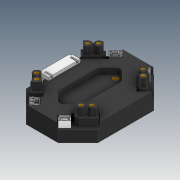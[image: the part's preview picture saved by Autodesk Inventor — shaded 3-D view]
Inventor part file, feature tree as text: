
AUTODESK INVENTOR PART (.ipt)
format: ipt  version: 2020 (Build 240168000, 168)  size: 708,608 bytes
history: native  units: mm
features: sketch x16, extrude x15, pattern_circular x4, projected_geometry x4, fillet x3, other x2, plane x1, mirror x1
ambient origin geometry x8: Origin, YZ Plane, XZ Plane, XY Plane, X Axis, Y Axis, Z Axis, Center Point
bodies: Solid1 (feature_tree)
feature tree (46):
  extrude  "Extrusion1"  Depth=60.0mm
  extrude  "Extrusion2"  Depth=20.0mm
  extrude  "Extrusion3"  Depth=5.3mm
  sketch  "Sketch4"  dims[d9=2.5mm]
  other  "Work Axis1"
  fillet  "Fillet1"  Radius=11.0mm
  fillet  "Fillet2"  Radius=8.5mm
  pattern_circular  "Circular Pattern1"  Count=2 Angle=270.0deg
  pattern_circular  "Circular Pattern2"  Count=2 Angle=360.0deg
  extrude  "Extrusion4"  Depth=5.8mm
  sketch  "Sketch6"  dims[d11=0.5mm]
  extrude  "Extrusion5"  Depth=4.15mm TaperAngle=0.0deg
  extrude  "Extrusion6"  Depth=0.3mm
  extrude  "Extrusion7"  Depth=1.0mm
  plane  "Work Plane1"
  mirror  "Mirror1"
  sketch  "Sketch8"  dims[d15=4.8mm]
  other  "Work Axis2"
  pattern_circular  "Circular Pattern3"  [2 undecoded]
  pattern_circular  "Circular Pattern4"  [2 undecoded]
  extrude  "Extrusion8"  Depth=1.6mm
  extrude  "Extrusion9"  Depth=0.3mm
  extrude  "Extrusion10"  Depth=0.3mm
  extrude  "Extrusion11"  Depth=0.3mm
  extrude  "Extrusion12"  Depth=0.3mm
  extrude  "Extrusion13"  Depth=0.3mm
  extrude  "Extrusion14"  Depth=0.6mm
  fillet  "Fillet3"  Radius=0.6mm
  extrude  "Extrusion15"  Depth=0.3mm
  sketch  "Sketch1"  dims[d0=45.0mm d1=60.0mm]
  sketch  "Sketch2"  dims[d2=20.0mm d3=35.0mm]
  sketch  "Sketch3"  dims[d4=6.8mm d5=0.0mm d6=5.3mm d7=11.0mm d8=8.5mm]
  projected_geometry  "Projected Loop1"
  sketch  "Sketch5"  dims[d10=2.0mm]
  projected_geometry  "Projected Loop2"
  sketch  "Sketch7"  dims[d12=5.2mm d13=0.0mm]
  sketch  "Sketch9"  dims[d16=2.5mm]
  sketch  "Sketch10"  dims[d17=0.5mm]
  projected_geometry  "Projected Loop3"
  sketch  "Sketch11"  dims[d18=5.2mm d19=0.0mm]
  sketch  "Sketch12"  dims[d20=0.2mm]
  sketch  "Sketch13"  dims[d21=0.2mm d22=20.0mm d23=270.0deg d25=20.0mm d26=360.0deg]
  sketch  "Sketch14"  dims[d28=1.5mm d29=5.8mm]
  projected_geometry  "Projected Loop4"
  sketch  "Sketch15"  dims[d30=4.5mm d31=4.15mm d32=0.0mm]
  sketch  "Sketch16"  dims[d34=0.3mm d35=0.3mm d36=1.0mm d37=0.6mm d40=2.2mm d41=1.6mm d42=0.3mm d43=0.3mm d44=0.3mm d45=0.3mm d46=0.3mm d47=0.3mm d48=0.6mm d49=0.6mm d50=0.3mm d51=4.15mm d52=0.0mm d53=3.0mm d54=0.0mm d55=0.6mm d56=0.8mm d57=0.3mm d58=0.0mm d59=20.0mm d60=270.0deg d62=20.0mm d63=360.0deg d65=20.0mm d66=6.0mm d67=0.5mm d68=5.6mm d69=0.0mm d70=0.5mm d71=1.24mm d72=12.0mm d73=3.86mm d74=19.0mm d75=0.5mm d76=4.36mm d77=5.6mm d78=0.0mm d79=1.0mm d80=1.5mm d81=2.0mm d82=5.6mm d83=0.0mm d84=1.0mm d85=1.0mm d86=1.0mm d87=1.0mm d88=5.6mm d89=0.0mm d90=2.0mm d91=0.5mm d92=1.5mm d93=0.0mm d94=7.6mm d95=0.3mm d97=0.3mm d98=0.3mm d99=0.3mm d100=0.3mm d101=0.3mm d102=4.0mm d103=0.0mm d104=15.0mm d105=25.0mm d106=4.0mm d107=0.0mm d108=3.0mm d109=32.0mm d110=3.5mm d111=0.0mm d112=0.0mm]
note: 4 required parameter values undecoded (feature->parameter linkage not recoverable at this tier; creation-order binding heuristic only, values carry confidence <= 0.55)
